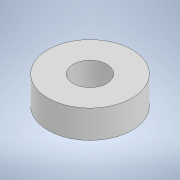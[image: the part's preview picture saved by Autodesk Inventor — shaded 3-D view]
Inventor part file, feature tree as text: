
AUTODESK INVENTOR PART (.ipt)
format: ipt  version: 2022 (Build 260153000, 153)  size: 96,256 bytes
history: native  units: mm
features: extrude x1, sketch x1
ambient origin geometry x8: Origin, YZ Plane, XZ Plane, XY Plane, X Axis, Y Axis, Z Axis, Center Point
bodies: Solid1 (feature_tree)
feature tree (2):
  extrude  "Extrusion1"  Depth=5.0mm
  sketch  "Sketch1"  dims[d0=6.0mm d1=15.0mm d2=5.0mm d3=0.0mm]
